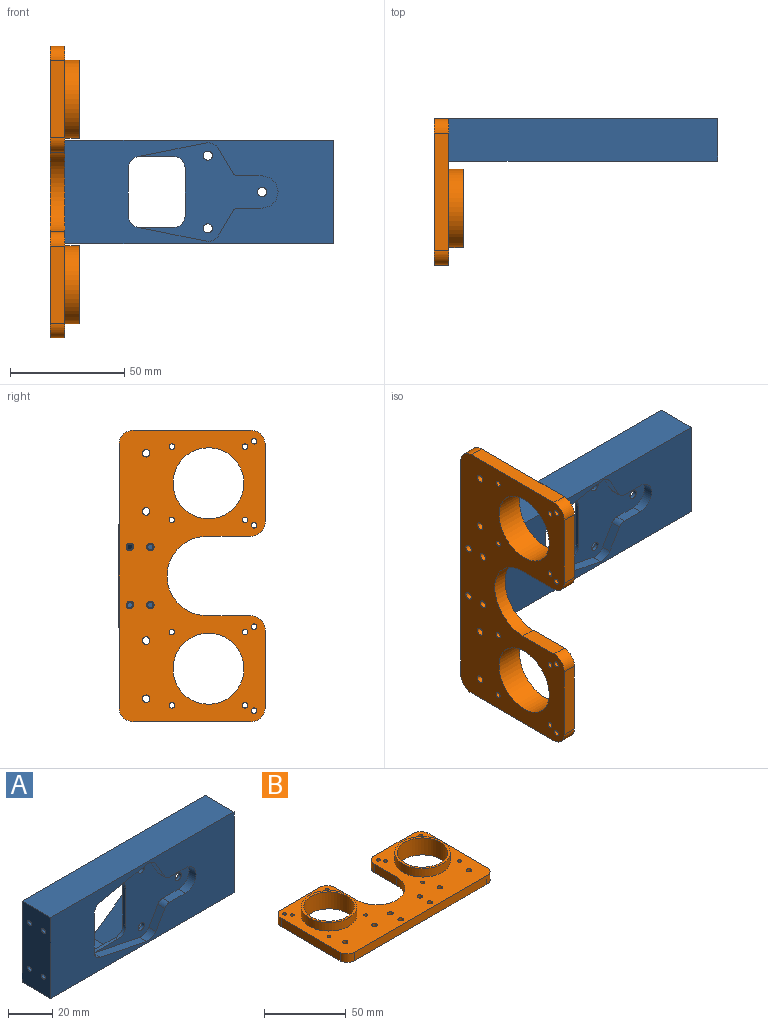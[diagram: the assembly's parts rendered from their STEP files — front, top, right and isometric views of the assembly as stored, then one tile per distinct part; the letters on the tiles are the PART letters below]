
ASSEMBLY  parts=2 mates=1
PART A: 55 faces, bbox 117.5x18.5x45 mm
  f0: plane 26.38x18.47mm, normal (0.57,0,-0.82), area 394.6mm2, adj f1,f2,f18,f49
  f1: plane 26.38x18.47mm, normal (-0.57,0,-0.82), area 394.6mm2, adj f0,f2,f18,f49
  f2: plane 52.77x12.25mm, normal (0,0,1), area 646.4mm2, adj f0,f1,f18,f49
  f3: plane 26.38x18.47mm, normal (0.57,0,0.82), area 394.6mm2, adj f4,f5,f15,f18
  f4: plane 52.77x12.25mm, normal (0,0,-1), area 646.4mm2, adj f3,f5,f15,f18
  f5: plane 26.38x18.47mm, normal (-0.57,0,0.82), area 394.6mm2, adj f3,f4,f15,f18
  f6: plane 38x12.25mm, normal (0,0,1), area 465.5mm2, adj f13,f16,f18,f48
  f7: plane 12.25x8.07mm, normal (0,0,1), area 98.8mm2, adj f8,f14,f17,f18
  f8: plane 28.56x20mm, normal (0.57,0,0.82), area 427.1mm2, adj f7,f9,f17,f18
  f9: plane 28.56x20mm, normal (0.57,0,-0.82), area 427.1mm2, adj f8,f10,f17,f18
  f10: plane 12.25x8.07mm, normal (0,0,-1), area 98.8mm2, adj f9,f14,f17,f18
  f11: plane 38x12.25mm, normal (0,0,-1), area 465.5mm2, adj f12,f16,f18,f48
  f12: plane 28.56x20mm, normal (-0.57,0,-0.82), area 427.1mm2, adj f11,f13,f16,f18
  f13: plane 28.56x20mm, normal (-0.57,0,0.82), area 427.1mm2, adj f6,f12,f16,f18
  f14: plane 40x12.25mm, normal (-1,0,0), area 490mm2, adj f7,f10,f17,f18
  f15: plane 52.77x18.47mm, normal (0,1,0), area 474.8mm2, adj f3,f4,f5,f19
  f16: plane 66.56x40mm, normal (0,1,0), area 1347.1mm2, adj f6,f11,f12,f13,f22,f23,f24,f25
  f17: plane 40x36.63mm, normal (0,1,0), area 881.3mm2, adj f7,f8,f9,f10,f14,f21
  f18: plane 117.5x45mm, normal (0,1,0), area 1327.5mm2, adj f0,f1,f2,f3,f4,f5,f6,f7
  f19: cylinder r=2mm len=4mm, axis (0,1,0), area 22mm2, adj f15,f41
  f20: cylinder r=2mm len=4mm, axis (0,1,0), area 22mm2, adj f41,f49
  f21: cylinder r=2mm len=4mm, axis (0,1,0), area 22mm2, adj f17,f41
  f22: plane 21x1.75mm, normal (-1,0,0), area 36.8mm2, adj f16,f23,f26,f41
  f23: cylinder r=4.97mm len=4.99mm, axis (0,1,0), area 13.7mm2, adj f16,f22,f24,f41
  f24: plane 15.77x1.75mm, normal (0,0,-1), area 27.6mm2, adj f16,f23,f40,f41
  f25: plane 15.77x1.75mm, normal (0,0,1), area 27.6mm2, adj f16,f26,f28,f41
  f26: cylinder r=4.97mm len=4.99mm, axis (0,1,0), area 13.7mm2, adj f16,f22,f25,f41
  f27: plane 21x6.25mm, normal (1,0,0), area 131.2mm2, adj f16,f28,f40,f54
  f28: cylinder r=5mm len=6.25mm, axis (0,1,0), area 42.9mm2, adj f16,f25,f27,f29,f54
  f29: plane 29.64x5.99mm, normal (0.2,0,0.98), area 136.1mm2, adj f28,f30,f41,f54
  f30: cylinder r=5.6mm len=5.96mm, axis (0,1,0), area 31.4mm2, adj f29,f31,f41,f54
  f31: plane 9.95x5.74mm, normal (-0.87,0,0.5), area 51.7mm2, adj f30,f32,f41,f54
  f32: cylinder r=3.5mm len=4.5mm, axis (0,1,0), area 16.5mm2, adj f31,f33,f41,f54
  f33: plane 10.03x4.5mm, normal (0,0,1), area 45.1mm2, adj f32,f34,f41,f54
  f34: cylinder r=7mm len=14mm, axis (0,1,0), area 99mm2, adj f33,f35,f41,f54
  f35: plane 10.05x4.5mm, normal (0,0,-1), area 45.2mm2, adj f34,f36,f41,f54
  f36: cylinder r=3.5mm len=4.5mm, axis (0,1,0), area 16.5mm2, adj f35,f37,f41,f54
  f37: plane 10.35x5.98mm, normal (-0.87,0,-0.5), area 53.8mm2, adj f36,f38,f41,f54
  f38: cylinder r=5.6mm len=5.26mm, axis (0,1,0), area 27.2mm2, adj f37,f39,f41,f54
  f39: plane 30.08x6.06mm, normal (0.2,0,-0.98), area 138.1mm2, adj f38,f40,f41,f54
  f40: cylinder r=5mm len=6.25mm, axis (0,1,0), area 42.9mm2, adj f16,f24,f27,f39,f54
  f41: plane 61.4x43mm, normal (0,-1,0), area 1090.4mm2, adj f19,f20,f21,f22,f23,f24,f25,f26
  f42: cylinder r=1.21mm len=6.65mm, axis (1,0,0), area 50.4mm2, adj f48,f50
  f43: cylinder r=1.21mm len=8mm, axis (1,0,0), area 60.6mm2, adj f44,f50
  f44: plane 2.41x2.41mm, normal (-1,0,0), area 4.6mm2, adj f43
  f45: cylinder r=1.21mm len=6.65mm, axis (1,0,0), area 50.4mm2, adj f48,f50
  f46: cylinder r=1.21mm len=8mm, axis (1,0,0), area 60.6mm2, adj f47,f50
  f47: plane 2.41x2.41mm, normal (-1,0,0), area 4.6mm2, adj f46
  f48: plane 40x12.25mm, normal (1,0,0), area 480.9mm2, adj f6,f11,f16,f18,f42,f45
  f49: plane 52.77x18.47mm, normal (0,1,0), area 474.8mm2, adj f0,f1,f2,f20
  f50: plane 45x18.5mm, normal (-1,0,0), area 814.2mm2, adj f18,f42,f43,f45,f46,f51,f53,f54
  f51: plane 117.5x18.5mm, normal (0,0,-1), area 2173.7mm2, adj f18,f50,f52,f54
  f52: plane 45x18.5mm, normal (1,0,0), area 832.5mm2, adj f18,f51,f53,f54
  f53: plane 117.5x18.5mm, normal (0,0,1), area 2173.8mm2, adj f18,f50,f52,f54
  f54: plane 117.5x45mm, normal (0,-1,0), area 3415.3mm2, adj f27,f28,f29,f30,f31,f32,f33,f34
PART B: 42 faces, bbox 127.4x63.8x12.7 mm
  f0: plane 127.38x63.83mm, normal (0,0,-1), area 5089.5mm2, adj f2,f3,f4,f5,f6,f7,f8,f9
  f1: plane 127.38x63.83mm, normal (0,0,1), area 4778.2mm2, adj f2,f3,f4,f5,f6,f7,f8,f9
  f2: cylinder r=1.21mm len=6.35mm, axis (0,0,1), area 48.1mm2, adj f0,f1
  f3: cylinder r=1.21mm len=6.35mm, axis (0,0,1), area 48.1mm2, adj f0,f1
  f4: cylinder r=1.21mm len=6.35mm, axis (0,0,1), area 48.1mm2, adj f0,f1
  f5: cylinder r=1.21mm len=6.35mm, axis (0,0,1), area 48.1mm2, adj f0,f1
  f6: cylinder r=1.21mm len=6.35mm, axis (0,0,1), area 48.1mm2, adj f0,f1
  f7: cylinder r=1.21mm len=6.35mm, axis (0,0,1), area 48.1mm2, adj f0,f1
  f8: cylinder r=1.21mm len=6.35mm, axis (0,0,1), area 48.1mm2, adj f0,f1
  f9: cylinder r=1.21mm len=6.35mm, axis (0,0,1), area 48.1mm2, adj f0,f1
  f10: cylinder r=17.02mm len=34.04mm, axis (0,0,-1), area 679mm2, adj f1,f11
  f11: plane 34.04x34.04mm, normal (0,0,1), area 155.7mm2, adj f10,f12
  f12: cylinder r=15.49mm len=30.99mm, axis (0,0,-1), area 1236.4mm2, adj f0,f11
  f13: cylinder r=17.02mm len=34.04mm, axis (0,0,-1), area 679mm2, adj f1,f14
  f14: plane 34.04x34.04mm, normal (0,0,1), area 155.7mm2, adj f13,f15
  f15: cylinder r=15.49mm len=30.99mm, axis (0,0,-1), area 1236.4mm2, adj f0,f14
  f16: plane 33.66x6.35mm, normal (0,1,0), area 213.7mm2, adj f0,f1,f39,f40
  f17: plane 51.13x6.35mm, normal (1,0,0), area 324.7mm2, adj f0,f1,f37,f40
  f18: plane 114.68x6.35mm, normal (0,-1,0), area 728.2mm2, adj f0,f1,f36,f37
  f19: plane 51.13x6.35mm, normal (-1,0,0), area 324.7mm2, adj f0,f1,f36,f41
  f20: plane 33.66x6.35mm, normal (0,1,0), area 213.7mm2, adj f0,f1,f38,f41
  f21: plane 19.19x6.35mm, normal (1,0,0), area 121.9mm2, adj f0,f1,f22,f38
  f22: cylinder r=17.34mm len=34.67mm, axis (0,0,-1), area 345.8mm2, adj f0,f1,f21,f23
  f23: plane 19.19x6.35mm, normal (-1,0,0), area 121.9mm2, adj f0,f1,f22,f39
  f24: cylinder r=1.65mm len=6.35mm, axis (0,0,-1), area 65.9mm2, adj f0,f1
  f25: cylinder r=1.65mm len=6.35mm, axis (0,0,-1), area 65.9mm2, adj f0,f1
  f26: cylinder r=1.65mm len=6.35mm, axis (0,0,-1), area 65.9mm2, adj f0,f1
  f27: cylinder r=1.65mm len=6.35mm, axis (0,0,-1), area 65.9mm2, adj f0,f1
  f28: cylinder r=1.65mm len=6.35mm, axis (0,0,-1), area 65.9mm2, adj f0,f1
  f29: cylinder r=1.65mm len=6.35mm, axis (0,0,-1), area 65.9mm2, adj f0,f1
  f30: cylinder r=1.65mm len=6.35mm, axis (0,0,-1), area 65.9mm2, adj f0,f1
  f31: cylinder r=1.65mm len=6.35mm, axis (0,0,-1), area 65.9mm2, adj f0,f1
  f32: cylinder r=1.21mm len=6.35mm, axis (0,0,1), area 48.1mm2, adj f0,f1
  f33: cylinder r=1.21mm len=6.35mm, axis (0,0,1), area 48.1mm2, adj f0,f1
  f34: cylinder r=1.21mm len=6.35mm, axis (0,0,1), area 48.1mm2, adj f0,f1
  f35: cylinder r=1.21mm len=6.35mm, axis (0,0,1), area 48.1mm2, adj f0,f1
  f36: cylinder r=6.35mm len=6.35mm, axis (0,0,-1), area 63.3mm2, adj f0,f1,f18,f19
  f37: cylinder r=6.35mm len=6.35mm, axis (0,0,-1), area 63.3mm2, adj f0,f1,f17,f18
  f38: cylinder r=6.35mm len=6.35mm, axis (0,0,-1), area 63.3mm2, adj f0,f1,f20,f21
  f39: cylinder r=6.35mm len=6.35mm, axis (0,0,-1), area 63.3mm2, adj f0,f1,f16,f23
  f40: cylinder r=6.35mm len=6.35mm, axis (0,0,-1), area 63.3mm2, adj f0,f1,f16,f17
  f41: cylinder r=6.35mm len=6.35mm, axis (0,0,-1), area 63.3mm2, adj f0,f1,f19,f20
PLACE A t=(10.04,-38.45,2.39)mm
PLACE B rot(axis=(-0.71,0,-0.71),180deg) t=(-11.73,-43.22,2.39)mm
MATE revolute B.f26 <-> A.f42  axis (1,0,0) through (-48.71,-24.78,15.09)mm
